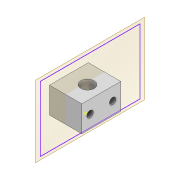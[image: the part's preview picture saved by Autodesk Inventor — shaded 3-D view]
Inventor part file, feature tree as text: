
AUTODESK INVENTOR PART (.ipt)
format: ipt  version: 2022 (Build 260153000, 153)  size: 121,344 bytes
history: native  units: mm
features: sketch x4, extrude x3, plane x1, projected_geometry x1
ambient origin geometry x8: Origin, YZ Plane, XZ Plane, XY Plane, X Axis, Y Axis, Z Axis, Center Point
bodies: Solid1 (feature_tree)
feature tree (9):
  extrude  "Extrusion1"  Depth=5.0mm
  plane  "Work Plane1"
  extrude  "Extrusion2"  Depth=6.0mm
  extrude  "Extrusion3"  Depth=8.0mm
  sketch  "Sketch6"  dims[d8=1.745329mm d9=4.1mm d10=100.0mm d11=0.0mm d12=4.2mm d13=2.0mm d14=2.0mm d15=2.5mm d16=2.5mm d17=4.0mm d18=4.0mm d19=100.0mm d20=0.0mm]
  sketch  "Sketch1"  dims[d0=4.0mm d2=5.0mm]
  sketch  "Sketch4"  dims[d3=6.0mm d4=6.0mm]
  sketch  "Sketch5"  dims[d5=8.0mm d6=0.0mm d7=5.0mm]
  projected_geometry  "Projected Loop1"
